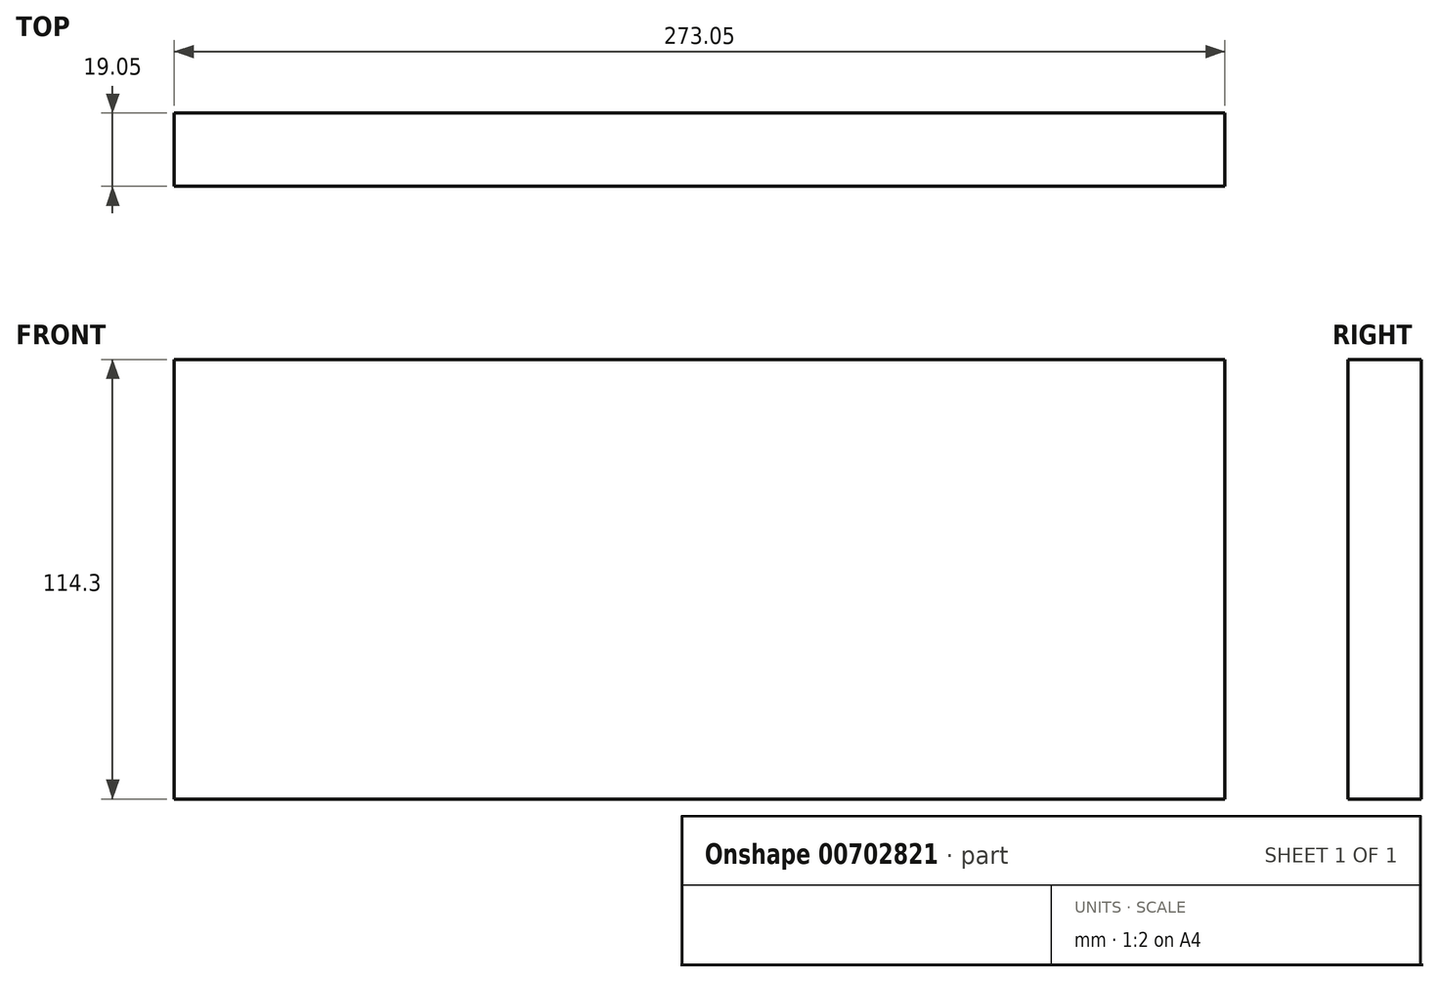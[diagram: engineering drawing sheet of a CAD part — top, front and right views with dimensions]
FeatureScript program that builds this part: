
annotation { "Feature Type Name" : "Feature", "Feature Type Description" : "" }
export const myFeature = defineFeature(function(context is Context, id is Id, definition is map)
    precondition{}
    {
        {
            var Q0;
            Q0=qCreatedBy(makeId("Front.planeOp"),FACE);
            var sketch = newSketch(context, id + "F0", { "sketchPlane" : qUnion([Q0])});
            skLineSegment(sketch, "E0.bottom", {"start": v(0, 0) * mm, "end": v(273.05, 0) * mm});
            skLineSegment(sketch, "E0.top", {"start": v(0, 114.3) * mm, "end": v(273.05, 114.3) * mm});
            skLineSegment(sketch, "E0.left", {"start": v(0, 0) * mm, "end": v(0, 114.3) * mm});
            skLineSegment(sketch, "E0.right", {"start": v(273.05, 0) * mm, "end": v(273.05, 114.3) * mm});
            skSolve(sketch);
        }
        {
            var Q0;
            Q0=makeQuery(id+"F0.imprint","IMPRINT",FACE,{"disambiguationData":[TD([[makeQuery(id+"F0.imprint","IMPRINT",EDGE,{"derivedFrom":sQuery(id+"F0.wireOp",EDGE,"E0.bottom")}),1.0]])]});
            extrude(context, id + "F1", {"entities" : qUnion([Q0]), "depth" : 19.05 * mm, "offsetDistance" : 25.4 * mm});
        }
    });
